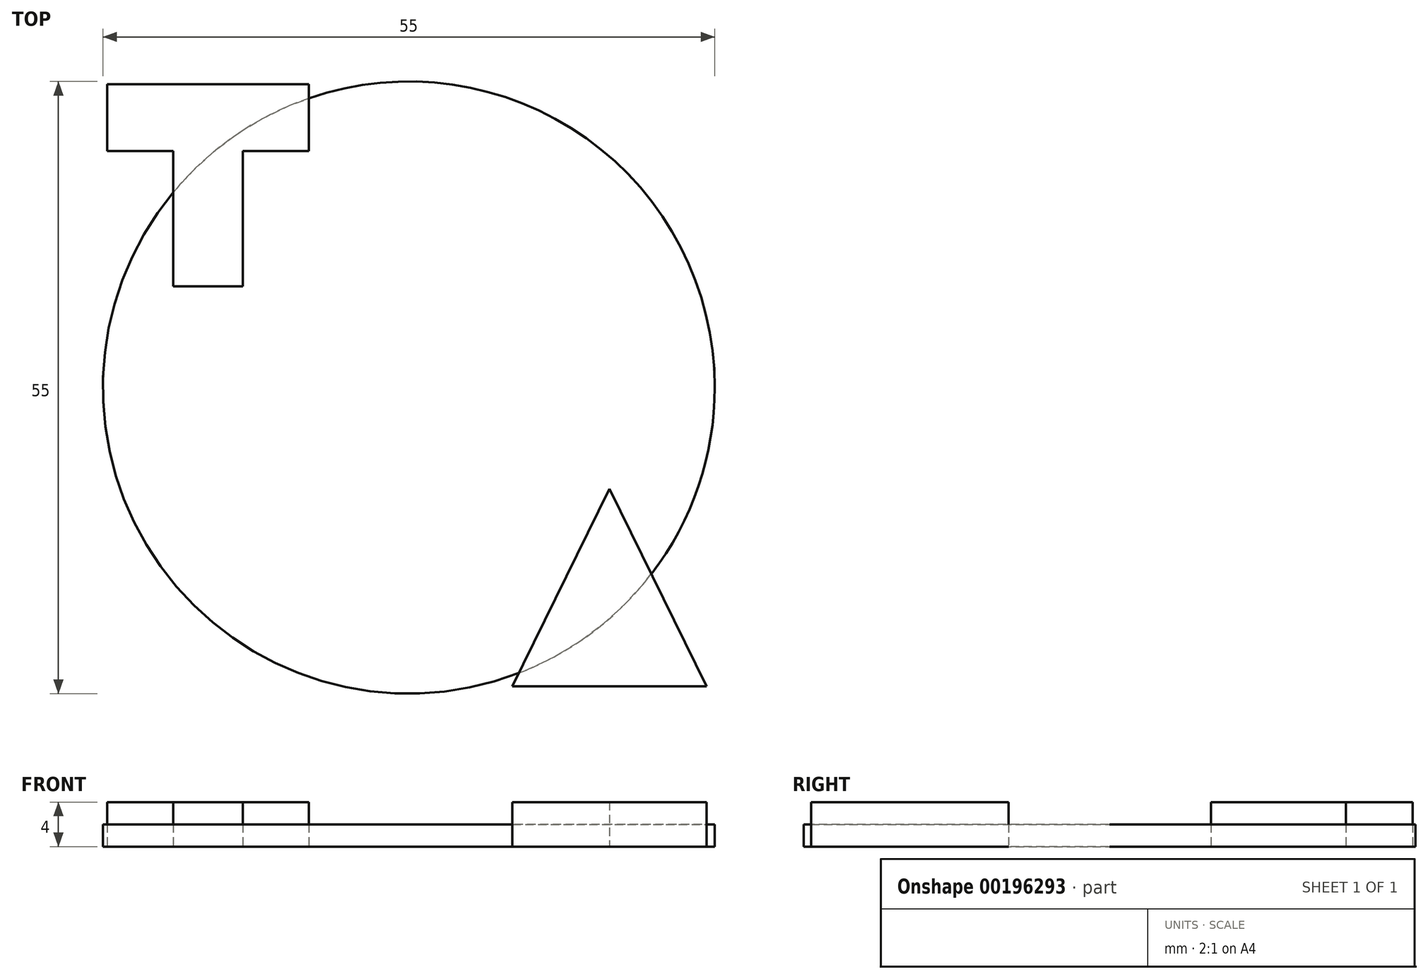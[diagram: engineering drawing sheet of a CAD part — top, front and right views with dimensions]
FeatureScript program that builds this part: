
annotation { "Feature Type Name" : "Feature", "Feature Type Description" : "" }
export const myFeature = defineFeature(function(context is Context, id is Id, definition is map)
    precondition{}
    {
        {
            var Q0;
            Q0=qCreatedBy(makeId("Top.planeOp"),FACE);
            var sketch = newSketch(context, id + "F0", { "sketchPlane" : qUnion([Q0])});
            skCircle(sketch, "E0", {"center": v(0, 0) * mm, "radius": 27.5 * mm});
            skSolve(sketch);
        }
        {
            var Q0;
            Q0=qCreatedBy(makeId("Top.planeOp"),FACE);
            var sketch = newSketch(context, id + "F1", { "sketchPlane" : qUnion([Q0])});
            skLineSegment(sketch, "E1", {"start": v(18.04, -9.09) * mm, "end": v(26.75, -26.85) * mm});
            skLineSegment(sketch, "E2", {"start": v(26.75, -26.85) * mm, "end": v(9.32, -26.85) * mm});
            skLineSegment(sketch, "E3", {"start": v(9.32, -26.85) * mm, "end": v(18.04, -9.09) * mm});
            skLineSegment(sketch, "E4", {"start": v(-27.13, 27.24) * mm, "end": v(-8.99, 27.24) * mm});
            skLineSegment(sketch, "E5", {"start": v(-8.99, 27.24) * mm, "end": v(-8.99, 21.24) * mm});
            skLineSegment(sketch, "E6", {"start": v(-8.99, 21.24) * mm, "end": v(-14.93, 21.24) * mm});
            skLineSegment(sketch, "E7", {"start": v(-14.93, 21.24) * mm, "end": v(-14.93, 9.1) * mm});
            skLineSegment(sketch, "E8", {"start": v(-14.93, 9.1) * mm, "end": v(-21.18, 9.1) * mm});
            skLineSegment(sketch, "E9", {"start": v(-21.18, 9.1) * mm, "end": v(-21.18, 21.24) * mm});
            skLineSegment(sketch, "E10", {"start": v(-21.18, 21.24) * mm, "end": v(-27.13, 21.24) * mm});
            skLineSegment(sketch, "E11", {"start": v(-27.13, 21.24) * mm, "end": v(-27.13, 27.24) * mm});
            skSolve(sketch);
        }
        {
            var Q0;
            Q0=makeQuery(id+"F0.imprint","IMPRINT",FACE,{"disambiguationData":[TD([[makeQuery(id+"F0.imprint","IMPRINT",EDGE,{"derivedFrom":sQuery(id+"F0.wireOp",EDGE,"E0")}),1.0]])]});
            var Q1;
            Q1=sQuery(id+"F0.wireOp",EDGE,"E0");
            extrude(context, id + "F2", {"entities" : qUnion([Q0]), "surfaceEntities" : qUnion([Q1]), "depth" : 2 * mm});
        }
        {
            var Q0;
            Q0=makeQuery(id+"F1.imprint","IMPRINT",FACE,{"disambiguationData":[TD([[makeQuery(id+"F1.imprint","IMPRINT",EDGE,{"derivedFrom":sQuery(id+"F1.wireOp",EDGE,"E4")}),-1.0]])]});
            extrude(context, id + "F3", {"entities" : qUnion([Q0]), "depth" : 4 * mm});
        }
        {
            var Q0;
            Q0=makeQuery(id+"F1.imprint","IMPRINT",FACE,{"disambiguationData":[TD([[makeQuery(id+"F1.imprint","IMPRINT",EDGE,{"derivedFrom":sQuery(id+"F1.wireOp",EDGE,"E1")}),-1.0]])]});
            extrude(context, id + "F4", {"entities" : qUnion([Q0]), "depth" : 4 * mm});
        }
    });
